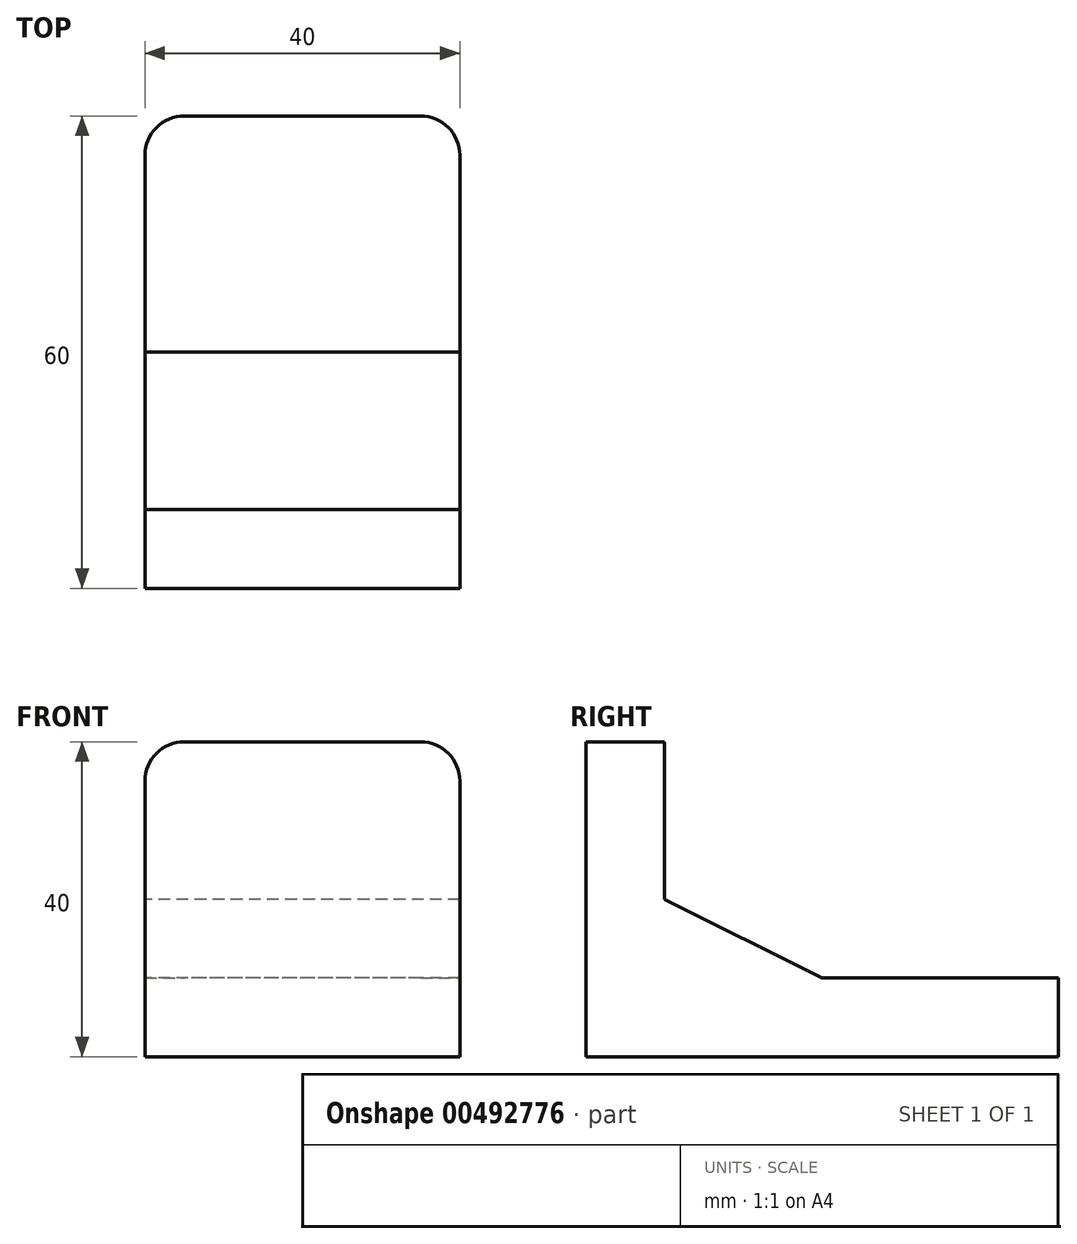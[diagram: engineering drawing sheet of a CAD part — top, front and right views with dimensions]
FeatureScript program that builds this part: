
annotation { "Feature Type Name" : "Feature", "Feature Type Description" : "" }
export const myFeature = defineFeature(function(context is Context, id is Id, definition is map)
    precondition{}
    {
        {
            var Q0;
            Q0=qCreatedBy(makeId("Right.planeOp"),FACE);
            var sketch = newSketch(context, id + "F0", { "sketchPlane" : qUnion([Q0])});
            skLineSegment(sketch, "E0", {"start": v(0, 0) * mm, "end": v(60, 0) * mm});
            skLineSegment(sketch, "E1", {"start": v(60, 0) * mm, "end": v(60, 10) * mm});
            skLineSegment(sketch, "E2", {"start": v(0, 0) * mm, "end": v(0, 40) * mm});
            skLineSegment(sketch, "E3", {"start": v(0, 40) * mm, "end": v(10, 40) * mm});
            skLineSegment(sketch, "E4", {"start": v(10, 40) * mm, "end": v(10, 20) * mm});
            skLineSegment(sketch, "E5", {"start": v(60, 10) * mm, "end": v(30, 10) * mm});
            skLineSegment(sketch, "E6", {"start": v(30, 10) * mm, "end": v(10, 20) * mm});
            skSolve(sketch);
        }
        {
            var Q0;
            Q0=makeQuery(id+"F0.imprint","IMPRINT",FACE,{"disambiguationData":[TD([[makeQuery(id+"F0.imprint","IMPRINT",EDGE,{"derivedFrom":sQuery(id+"F0.wireOp",EDGE,"E0")}),1.0]])]});
            extrude(context, id + "F1", {"entities" : qUnion([Q0]), "depth" : 40 * mm});
        }
        {
            var Q0;
            Q0=makeQuery(id+"F1.opExtrude","CAP_EDGE",EDGE,{"disambiguationData":[OSD([sQuery(id+"F0.wireOp",EDGE,"E3")])],"isStart":false});
            var Q1;
            Q1=makeQuery(id+"F1.opExtrude","CAP_EDGE",EDGE,{"disambiguationData":[OSD([sQuery(id+"F0.wireOp",EDGE,"E3")])],"isStart":true});
            var Q2;
            Q2=makeQuery(id+"F1.opExtrude","CAP_EDGE",EDGE,{"disambiguationData":[OSD([sQuery(id+"F0.wireOp",EDGE,"E1")])],"isStart":false});
            var Q3;
            Q3=makeQuery(id+"F1.opExtrude","CAP_EDGE",EDGE,{"disambiguationData":[OSD([sQuery(id+"F0.wireOp",EDGE,"E1")])],"isStart":true});
            fillet(context, id + "F2", {"entities" : qUnion([Q0, Q1, Q2, Q3]), "radius" : 5 * mm, "tangentPropagation" : true, "allowEdgeOverflow" : false});
        }
    });
